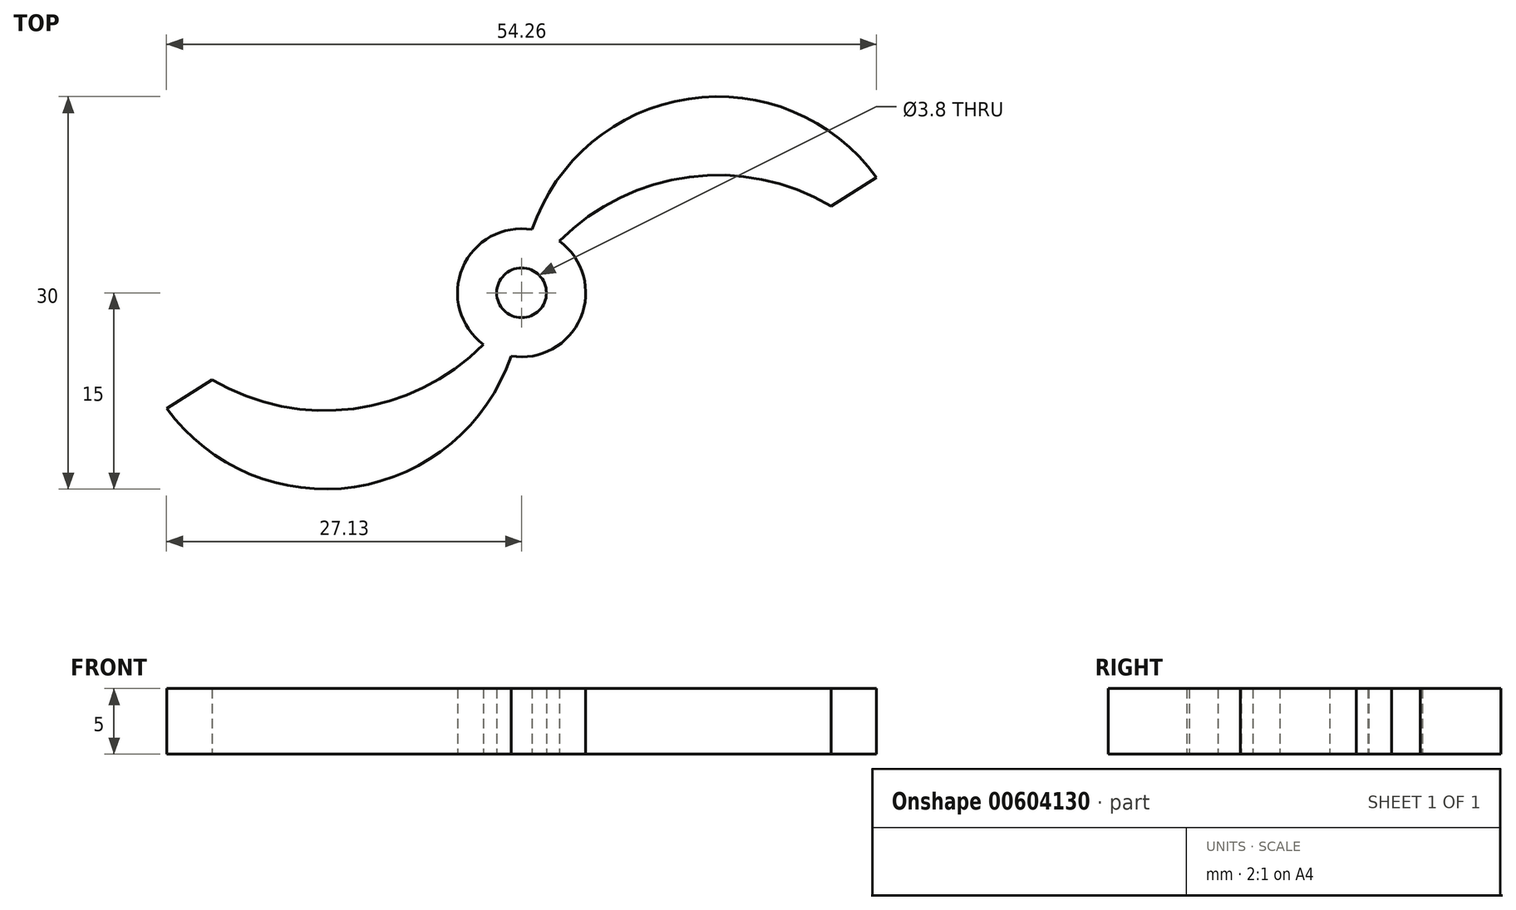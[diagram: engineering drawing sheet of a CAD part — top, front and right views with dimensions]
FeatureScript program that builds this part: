
annotation { "Feature Type Name" : "Feature", "Feature Type Description" : "" }
export const myFeature = defineFeature(function(context is Context, id is Id, definition is map)
    precondition{}
    {
        {
            var Q0;
            Q0=qCreatedBy(makeId("Top.planeOp"),FACE);
            var sketch = newSketch(context, id + "F0", { "sketchPlane" : qUnion([Q0])});
            skCircle(sketch, "E0", {"center": v(0, 0) * mm, "radius": 1.9 * mm});
            skArc(sketch, "E1", {"start": v(-30, 0) * mm, "mid": v(-15, -15) * mm, "end": v(0, 0) * mm});
            skArc(sketch, "E2", {"start": v(30, 0) * mm, "mid": v(15, 15) * mm, "end": v(0, 0) * mm});
            skCircle(sketch, "E3", {"center": v(0, 0) * mm, "radius": 4.9 * mm});
            skArc(sketch, "E4", {"start": v(-30, 0) * mm, "mid": v(-15, -9) * mm, "end": v(0, 0) * mm});
            skArc(sketch, "E5", {"start": v(30, 0) * mm, "mid": v(15, 9) * mm, "end": v(0, 0) * mm});
            skLineSegment(sketch, "E6", {"start": v(-35.06, -30.38) * mm, "end": v(39.06, 16.35) * mm});
            skLineSegment(sketch, "E7", {"start": v(-39.36, -16.54) * mm, "end": v(39.06, 32.9) * mm});
            skSolve(sketch);
        }
        {
            var Q0;
            {var subQ0=sQuery(id+"F0.wireOp",EDGE,"E7");var subQ5=sQuery(id+"F0.wireOp",EDGE,"E1");var subQ7=makeQuery(id+"F0.imprint","INTERSECT",VERTEX,{"derivedFrom":[subQ5,subQ0]});Q0=makeQuery(id+"F0.imprint","IMPRINT",FACE,{"disambiguationData":[TD([[makeQuery(id+"F0.imprint","IMPRINT",EDGE,{"disambiguationData":[TD([[subQ7,-1.0]])],"derivedFrom":subQ5}),1.0]])]});}
            var Q1;
            {var subQ0=sQuery(id+"F0.wireOp",EDGE,"E4");var subQ1=sQuery(id+"F0.wireOp",EDGE,"E0");var subQ2=makeQuery(id+"F0.imprint","INTERSECT",VERTEX,{"derivedFrom":[subQ1,subQ0]});Q1=makeQuery(id+"F0.imprint","IMPRINT",FACE,{"disambiguationData":[TD([[makeQuery(id+"F0.imprint","IMPRINT",EDGE,{"disambiguationData":[TD([[subQ2,-1.0]])],"derivedFrom":subQ1}),-1.0]])]});}
            var Q2;
            {var subQ0=sQuery(id+"F0.wireOp",EDGE,"E5");var subQ1=sQuery(id+"F0.wireOp",EDGE,"E0");var subQ2=makeQuery(id+"F0.imprint","INTERSECT",VERTEX,{"derivedFrom":[subQ1,subQ0]});Q2=makeQuery(id+"F0.imprint","IMPRINT",FACE,{"disambiguationData":[TD([[makeQuery(id+"F0.imprint","IMPRINT",EDGE,{"disambiguationData":[TD([[subQ2,1.0]])],"derivedFrom":subQ1}),-1.0]])]});}
            var Q3;
            {var subQ0=sQuery(id+"F0.wireOp",EDGE,"E2");var subQ1=sQuery(id+"F0.wireOp",EDGE,"E0");var subQ2=makeQuery(id+"F0.imprint","INTERSECT",VERTEX,{"derivedFrom":[subQ1,subQ0]});Q3=makeQuery(id+"F0.imprint","IMPRINT",FACE,{"disambiguationData":[TD([[makeQuery(id+"F0.imprint","IMPRINT",EDGE,{"disambiguationData":[TD([[subQ2,-1.0]])],"derivedFrom":subQ1}),-1.0]])]});}
            var Q4;
            {var subQ0=sQuery(id+"F0.wireOp",EDGE,"E2");var subQ1=sQuery(id+"F0.wireOp",EDGE,"E0");var subQ2=makeQuery(id+"F0.imprint","INTERSECT",VERTEX,{"derivedFrom":[subQ1,subQ0]});Q4=makeQuery(id+"F0.imprint","IMPRINT",FACE,{"disambiguationData":[TD([[makeQuery(id+"F0.imprint","IMPRINT",EDGE,{"disambiguationData":[TD([[subQ2,1.0]])],"derivedFrom":subQ1}),-1.0]])]});}
            var Q5;
            {var subQ0=sQuery(id+"F0.wireOp",EDGE,"E6");var subQ5=sQuery(id+"F0.wireOp",EDGE,"E2");var subQ8=makeQuery(id+"F0.imprint","INTERSECT",VERTEX,{"derivedFrom":[subQ5,subQ0]});Q5=makeQuery(id+"F0.imprint","IMPRINT",FACE,{"disambiguationData":[TD([[makeQuery(id+"F0.imprint","IMPRINT",EDGE,{"disambiguationData":[TD([[subQ8,-1.0]])],"derivedFrom":subQ5}),1.0]])]});}
            extrude(context, id + "F1", {"entities" : qUnion([Q0, Q1, Q2, Q3, Q4, Q5]), "depth" : 5 * mm, "offsetDistance" : 25 * mm});
        }
    });
